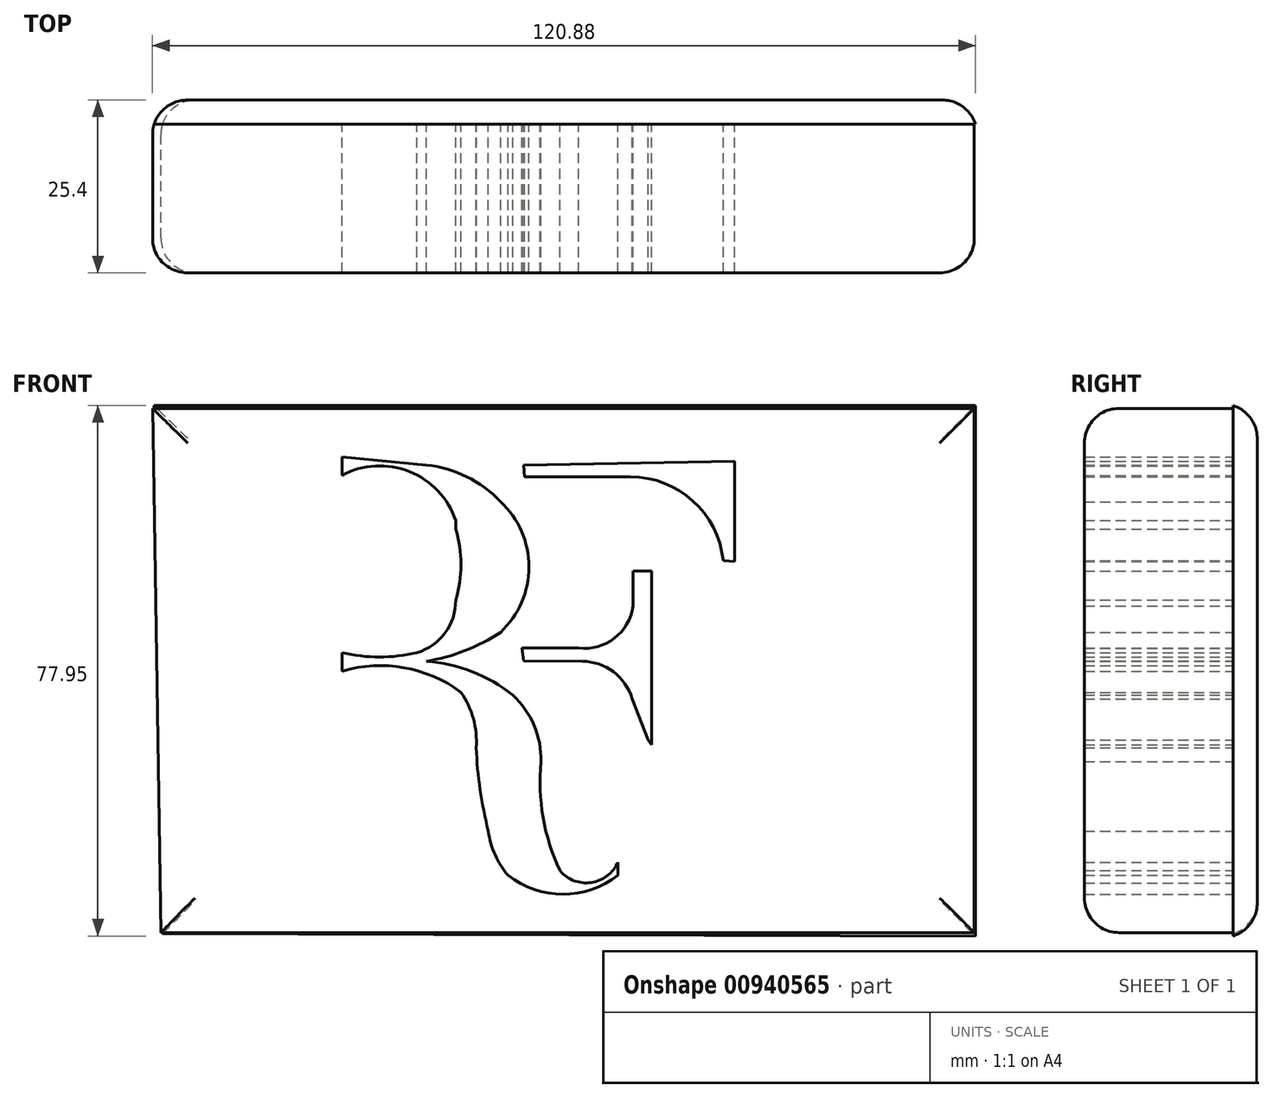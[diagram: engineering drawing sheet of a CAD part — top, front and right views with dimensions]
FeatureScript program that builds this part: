
annotation { "Feature Type Name" : "Feature", "Feature Type Description" : "" }
export const myFeature = defineFeature(function(context is Context, id is Id, definition is map)
    precondition{}
    {
        {
            var Q0;
            Q0=qCreatedBy(makeId("Front.planeOp"),FACE);
            var sketch = newSketch(context, id + "F0", { "sketchPlane" : qUnion([Q0])});
            skArc(sketch, "E0", {"start": v(-9.98, 22.12) * mm, "mid": v(-16.78, 29.33) * mm, "end": v(-26.67, 28.77) * mm});
            skArc(sketch, "E1", {"start": v(-9.98, 10.45) * mm, "mid": v(-9.2, 15.68) * mm, "end": v(-9.98, 20.9) * mm});
            skArc(sketch, "E2", {"start": v(-15.68, 2.71) * mm, "mid": v(-11.52, 5.62) * mm, "end": v(-9.98, 10.45) * mm});
            skLineSegment(sketch, "E3", {"start": v(-9.98, 22.12) * mm, "end": v(-9.98, 20.9) * mm});
            skArc(sketch, "E4", {"start": v(-26.67, 2.71) * mm, "mid": v(-21.17, 2.08) * mm, "end": v(-15.68, 2.71) * mm});
            skLineSegment(sketch, "E5", {"start": v(-26.67, 28.77) * mm, "end": v(-26.67, 31.49) * mm});
            skLineSegment(sketch, "E6", {"start": v(-26.67, 2.71) * mm, "end": v(-26.67, 0) * mm});
            skArc(sketch, "E7", {"start": v(-9.17, -3.1) * mm, "mid": v(-17.56, 0.5) * mm, "end": v(-26.67, 0) * mm});
            skArc(sketch, "E8", {"start": v(-6.97, -11.24) * mm, "mid": v(-7.38, -6.99) * mm, "end": v(-9.17, -3.1) * mm});
            skArc(sketch, "E9", {"start": v(-6.97, -11.24) * mm, "mid": v(-6.38, -17.43) * mm, "end": v(-5.17, -23.52) * mm});
            skArc(sketch, "E10", {"start": v(-5.17, -23.52) * mm, "mid": v(-4.2, -26.97) * mm, "end": v(-2.28, -30) * mm});
            skArc(sketch, "E11", {"start": v(-2.28, -30) * mm, "mid": v(5.8, -32.77) * mm, "end": v(13.86, -30) * mm});
            skLineSegment(sketch, "E12", {"start": v(13.86, -30) * mm, "end": v(13.86, -28.07) * mm});
            skArc(sketch, "E13", {"start": v(5.31, -29.31) * mm, "mid": v(9.93, -31.06) * mm, "end": v(13.86, -28.07) * mm});
            skArc(sketch, "E14", {"start": v(2.55, -13.31) * mm, "mid": v(2.86, -21.5) * mm, "end": v(5.31, -29.31) * mm});
            skArc(sketch, "E15", {"start": v(2.55, -13.31) * mm, "mid": v(1.54, -7.97) * mm, "end": v(-1.59, -3.52) * mm});
            skArc(sketch, "E16", {"start": v(-1.59, -3.52) * mm, "mid": v(-7.56, -0.08) * mm, "end": v(-14.28, 1.45) * mm});
            skArc(sketch, "E17", {"start": v(-14.28, 1.45) * mm, "mid": v(-8.6, 3.02) * mm, "end": v(-3.38, 5.72) * mm});
            skArc(sketch, "E18", {"start": v(-3.38, 5.72) * mm, "mid": v(0.79, 15.31) * mm, "end": v(-3.38, 24.9) * mm});
            skArc(sketch, "E19", {"start": v(-3.38, 24.9) * mm, "mid": v(-8.35, 28.57) * mm, "end": v(-14.28, 30.28) * mm});
            skLineSegment(sketch, "E20", {"start": v(-14.28, 30.28) * mm, "end": v(-26.67, 31.49) * mm});
            skLineSegment(sketch, "E21", {"start": v(0, 30.28) * mm, "end": v(0.14, 28.57) * mm});
            skPoint(sketch, "E21.endSnap0", {"position": v(-8.35, 28.57) * mm});
            skArc(sketch, "E22", {"start": v(8.07, 3.38) * mm, "mid": v(13.35, 4.84) * mm, "end": v(16.07, 9.59) * mm});
            skArc(sketch, "E23", {"start": v(15.93, -4.07) * mm, "mid": v(13.2, -0.1) * mm, "end": v(8.62, 1.45) * mm});
            skLineSegment(sketch, "E24", {"start": v(18.83, 14.7) * mm, "end": v(18.83, -10.83) * mm});
            skLineSegment(sketch, "E25", {"start": v(18.83, -10.83) * mm, "end": v(18.28, -10.14) * mm});
            skLineSegment(sketch, "E26", {"start": v(18.28, -10.14) * mm, "end": v(15.93, -4.07) * mm});
            skLineSegment(sketch, "E27", {"start": v(8.62, 1.45) * mm, "end": v(0, 1.47) * mm});
            skLineSegment(sketch, "E28", {"start": v(0, 1.47) * mm, "end": v(-0.23, 3.38) * mm});
            skLineSegment(sketch, "E29", {"start": v(-0.23, 3.38) * mm, "end": v(8.07, 3.38) * mm});
            skLineSegment(sketch, "E30", {"start": v(29.31, 16.2) * mm, "end": v(30.98, 16.08) * mm});
            skLineSegment(sketch, "E31", {"start": v(30.98, 16.08) * mm, "end": v(30.98, 30.83) * mm});
            skLineSegment(sketch, "E32", {"start": v(30.98, 30.83) * mm, "end": v(0, 30.28) * mm});
            skLineSegment(sketch, "E33", {"start": v(0.14, 28.57) * mm, "end": v(15.66, 28.57) * mm});
            skLineSegment(sketch, "E34", {"start": v(15.66, 28.57) * mm, "end": v(15.66, 29.45) * mm});
            skLineSegment(sketch, "E35", {"start": v(-54.5, 38.6) * mm, "end": v(-53.28, -38.42) * mm});
            skLineSegment(sketch, "E36", {"start": v(-53.28, -38.42) * mm, "end": v(66.2, -38.42) * mm});
            skLineSegment(sketch, "E37", {"start": v(66.2, -38.42) * mm, "end": v(66.2, 38.6) * mm});
            skLineSegment(sketch, "E38", {"start": v(66.2, 38.6) * mm, "end": v(-54.5, 38.6) * mm});
            skLineSegment(sketch, "E39", {"start": v(16.07, 9.59) * mm, "end": v(16.07, 14.7) * mm});
            skLineSegment(sketch, "E40", {"start": v(16.07, 14.7) * mm, "end": v(18.83, 14.7) * mm});
            skArc(sketch, "E41", {"start": v(29.31, 16.2) * mm, "mid": v(24.87, 25.02) * mm, "end": v(15.66, 28.57) * mm});
            skSolve(sketch);
        }
        {
            var Q0;
            Q0 = qSketchRegion(id + "F0", true);
            extrude(context, id + "F1", {"entities" : qUnion([Q0]), "depth" : 25.4 * mm, "offsetDistance" : 25.4 * mm});
        }
        {
            var Q0;
            Q0=qCreatedBy(makeId("Front.planeOp"),FACE);
            var sketch = newSketch(context, id + "F2", { "sketchPlane" : qUnion([Q0])});
            skLineSegment(sketch, "E42", {"start": v(-53.22, -38.57) * mm, "end": v(-54.5, 39.03) * mm});
            skLineSegment(sketch, "E43", {"start": v(-54.5, 39.03) * mm, "end": v(66.37, 39.03) * mm});
            skLineSegment(sketch, "E44", {"start": v(66.37, 39.03) * mm, "end": v(66.37, -38.92) * mm});
            skLineSegment(sketch, "E45", {"start": v(66.37, -38.92) * mm, "end": v(-53.22, -38.57) * mm});
            skSolve(sketch);
        }
        {
            var Q0;
            Q0=makeQuery(id+"F2.imprint","IMPRINT",FACE,{"disambiguationData":[TD([[makeQuery(id+"F2.imprint","IMPRINT",EDGE,{"derivedFrom":sQuery(id+"F2.wireOp",EDGE,"E42")}),-1.0]])]});
            extrude(context, id + "F3", {"entities" : qUnion([Q0]), "operationType" : NewBodyOperationType.ADD, "depth" : 3.56 * mm, "offsetDistance" : 25.4 * mm});
        }
        {
            var Q0;
            Q0=makeQuery(id+"F1.opExtrude","CAP_EDGE",EDGE,{"disambiguationData":[OSD([sQuery(id+"F0.wireOp",EDGE,"E38")])],"isStart":false});
            var Q1;
            Q1=makeQuery(id+"F1.opExtrude","CAP_EDGE",EDGE,{"disambiguationData":[OSD([sQuery(id+"F0.wireOp",EDGE,"E36")])],"isStart":false});
            var Q2;
            Q2=makeQuery(id+"F1.opExtrude","CAP_EDGE",EDGE,{"disambiguationData":[OSD([sQuery(id+"F0.wireOp",EDGE,"E37")])],"isStart":false});
            var Q3;
            Q3=makeQuery(id+"F1.opExtrude","CAP_EDGE",EDGE,{"disambiguationData":[OSD([sQuery(id+"F0.wireOp",EDGE,"E35")])],"isStart":false});
            var Q4;
            Q4=makeQuery(id+"F1.opExtrude","CAP_EDGE",EDGE,{"disambiguationData":[OSD([sQuery(id+"F0.wireOp",EDGE,"E35")])],"isStart":true});
            var Q5;
            Q5=makeQuery(id+"F3.opExtrude","CAP_EDGE",EDGE,{"disambiguationData":[OSD([sQuery(id+"F2.wireOp",EDGE,"E43")])],"isStart":true});
            var Q6;
            Q6=makeQuery(id+"F3.opExtrude","CAP_EDGE",EDGE,{"disambiguationData":[OSD([sQuery(id+"F2.wireOp",EDGE,"E44")])],"isStart":true});
            var Q7;
            Q7=makeQuery(id+"F3.opExtrude","CAP_EDGE",EDGE,{"disambiguationData":[OSD([sQuery(id+"F2.wireOp",EDGE,"E45")])],"isStart":true});
            fillet(context, id + "F4", {"entities" : qUnion([Q0, Q1, Q2, Q3, Q4, Q5, Q6, Q7]), "radius" : 5.08 * mm, "tangentPropagation" : true, "allowEdgeOverflow" : false});
        }
    });
